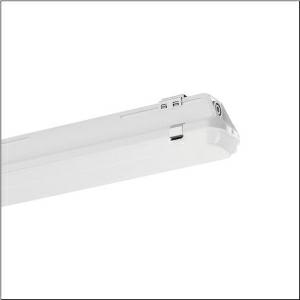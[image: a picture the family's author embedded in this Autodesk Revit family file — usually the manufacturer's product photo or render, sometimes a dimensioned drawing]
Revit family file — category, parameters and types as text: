
# Revit family: monsun_r__21_51fb20dp460b_2c2a
name_source: partatom
category: Lighting Fixtures
units: mm (PartAtom-declared; Revit-internal decimal feet)

## family parameters
Cut with Voids When Loaded = No
Host = Face
Light Source = No
Part Type = Normal
Room Calculation Point = No
Round Connector Dimension = Use Diameter
Shared = No

## types (1)
- --- (1 x LED, 5460 lm, 39.4 W, 4000K)
    Apparent Load = 39 VA
    CIE Flux Codes = 45 75 93 94 100
    Color Rendering = 80
    Color Temperature = 4000K
    Default Elevation = 1800 mm
    Description = Monsun® 21, damp-proof luminaire, chain hanger, primary optical cover: enclosure, of PC, light emission: direct distribution, primary light characteristic: symmetric, installation type: suspended mounting, surface-mounted, horizontal mounting, vertical mounting, LED, rated luminous flux: 5.460lm, luminous efficacy: 139lm/W, light colour: 840, colour temperature: 4000K, control gear: ECG DALI, with terminal, 5-pole, max. 2.5mm², mains connection: 220..240V, AC, 50/60Hz, rated input power: 39W, housing, of glass-fibre reinforced polyester, uncoated, bright grey, length: 1.590mm, width: 90mm, height: 88mm, clip for enclosure, of stainless steel (V2A), ceiling mounting element, of stainless steel (V2A), chain hanger, of stainless steel (V2A), protection rating (complete): IP66, insulation class (complete): insulation class I (protective earthing), certification: CE, ENEC, VDE, UKCA, protection symbol: D, impact resistance: IK08, permissible operating ambient temperature: -25..+35°C, standard: EN 50419, EN 60598-2-1, corresponds to IFS (International Featured Standards) requirements for safety and quality in the food industry, for indoor or canopied outdoor use, no direct snow, no direct sun, no direct rain, packaging unit: 1 piece
    Height = 89 mm
    Lamp = 1 x LED
    Lamp Light Flux = 5460 lm
    Lamp Power = 39.4 W
    Lamp count = 1
    Length = 1590 mm
    Luminous efficacy = 139 lm/W
    Manufacturer = Siteco
    ModVariant = No
    Model = 51FB20DP460B
    Mounting Place = Ceiling
    Mounting Type = Pendant
    Number of Poles = 1
    OnlyDefault = Yes
    Power Factor = 1
    Product Name = Monsun® 21
    Product group = damp-proof luminaire | ceiling pendant
    ProductGroupID = 908
    Protection Class = Protection class I
    Protection Degree = IP 66
    RLX_Detail_Level = 1
    RlxData = <blob elided: 91845 chars, md5=de69c9a6>
    Socket = socket
    Standby Power = 0 W
    System Light Flux = 5460 lm
    System Power = 39 W
    Type Comments = factory setting: luminous flux: 100 % | dim-lin: 254 | 261 mA
    Type Image = l_1006717.jpg
    URL = http://relux.com
    VarID = @adj_125021
    Voltage = 0 V
    Weight = 0.00 kg
    Width = 90 mm

## geometry (parser evidence)
native form markers: Blend x4, Sweep x14
no freeform markers — native parametric forms only
